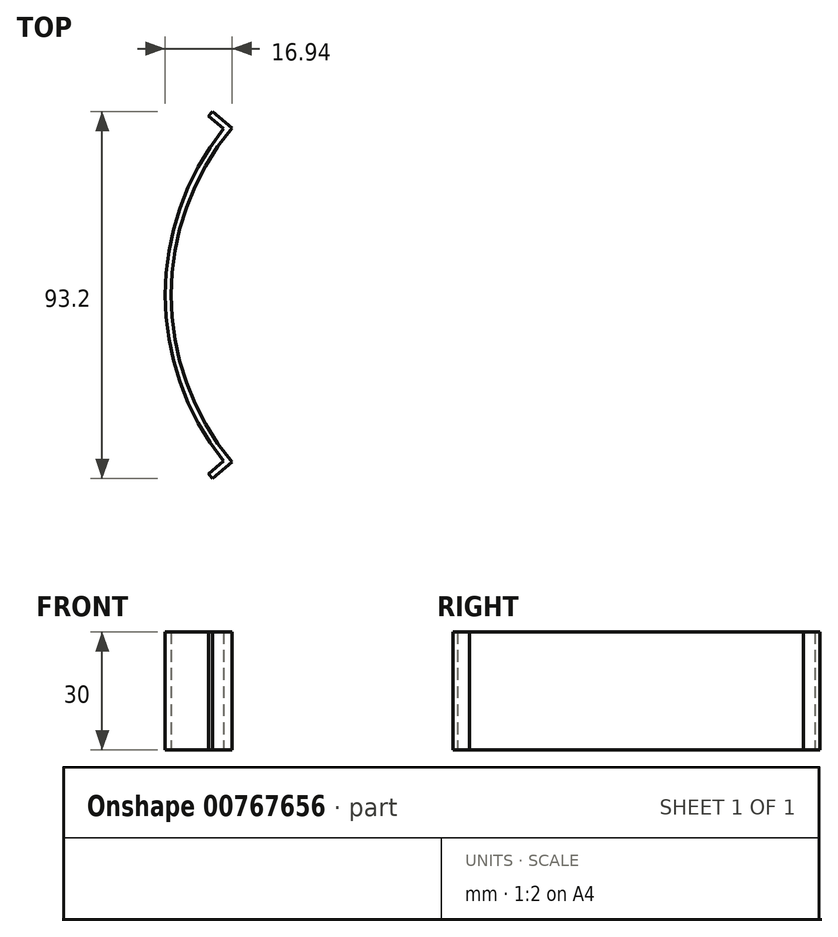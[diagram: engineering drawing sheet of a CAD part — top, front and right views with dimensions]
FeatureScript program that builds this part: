
annotation { "Feature Type Name" : "Feature", "Feature Type Description" : "" }
export const myFeature = defineFeature(function(context is Context, id is Id, definition is map)
    precondition{}
    {
        {
            var Q0;
            Q0=qCreatedBy(makeId("Top.planeOp"),FACE);
            var sketch = newSketch(context, id + "F0", { "sketchPlane" : qUnion([Q0])});
            skArc(sketch, "E0", {"start": v(-52.66, 42.23) * mm, "mid": v(-67.5, 0) * mm, "end": v(-52.66, -42.23) * mm});
            skArc(sketch, "E1", {"start": v(-50.56, 42.42) * mm, "mid": v(-66, 0) * mm, "end": v(-50.56, -42.42) * mm});
            skArc(sketch, "E2", {"start": v(-56.49, 45.44) * mm, "mid": v(-56.02, 46.02) * mm, "end": v(-55.54, 46.6) * mm});
            skLineSegment(sketch, "E3", {"start": v(-56.49, 45.44) * mm, "end": v(-52.66, 42.23) * mm});
            skLineSegment(sketch, "E4", {"start": v(-55.54, 46.6) * mm, "end": v(-50.56, 42.42) * mm});
            skLineSegment(sketch, "E5", {"start": v(-56.49, -45.44) * mm, "end": v(-52.66, -42.23) * mm});
            skLineSegment(sketch, "E6", {"start": v(-55.54, -46.6) * mm, "end": v(-50.56, -42.42) * mm});
            skArc(sketch, "E7", {"start": v(-56.49, -45.44) * mm, "mid": v(-56.02, -46.02) * mm, "end": v(-55.54, -46.6) * mm});
            skSolve(sketch);
        }
        {
            var Q0;
            Q0=makeQuery(id+"F0.imprint","IMPRINT",FACE,{"disambiguationData":[TD([[makeQuery(id+"F0.imprint","IMPRINT",EDGE,{"derivedFrom":sQuery(id+"F0.wireOp",EDGE,"E0")}),1.0]])]});
            extrude(context, id + "F1", {"entities" : qUnion([Q0]), "depth" : 30 * mm, "offsetDistance" : 25 * mm});
        }
    });
